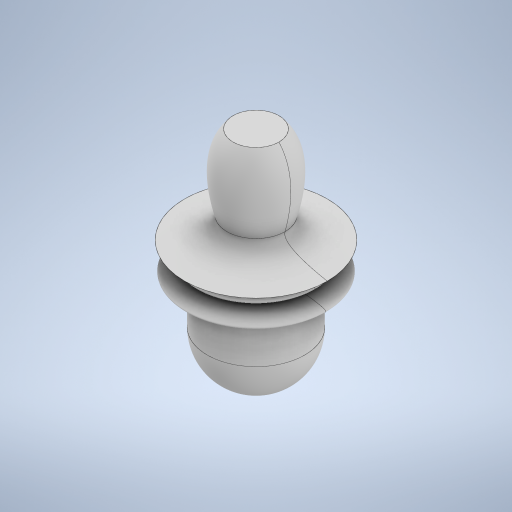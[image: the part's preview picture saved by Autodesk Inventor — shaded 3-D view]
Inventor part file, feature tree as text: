
AUTODESK INVENTOR PART (.ipt)
format: ipt  version: 2023 (Build 270158000, 158)  size: 462,336 bytes
history: native  units: in
note: dims shown in document units (in); Inventor stores cm internally (conversion verified against a paired STEP export)
features: revolve x2, sketch x2
ambient origin geometry x8: Origin, YZ Plane, XZ Plane, XY Plane, X Axis, Y Axis, Z Axis, Center Point
bodies: Solid1 (feature_tree)
feature tree (4):
  revolve  "Revolution1"  [1 undecoded]
  revolve  "Revolution2"  [1 undecoded]
  sketch  "Sketch1"  dims[d0=0.6693in d1=0.5906in]
  sketch  "Sketch2"  dims[d3=0.4455in d5=2.3574in d6=0.1271in d7=0.315in d8=1.0236in d9=0.1672in d10=0.1497in d13=0.3725in d14=0.3993in d15=90.0deg d16=90.0deg]
note: 2 required parameter values undecoded (feature->parameter linkage not recoverable at this tier; creation-order binding heuristic only, values carry confidence <= 0.55)
